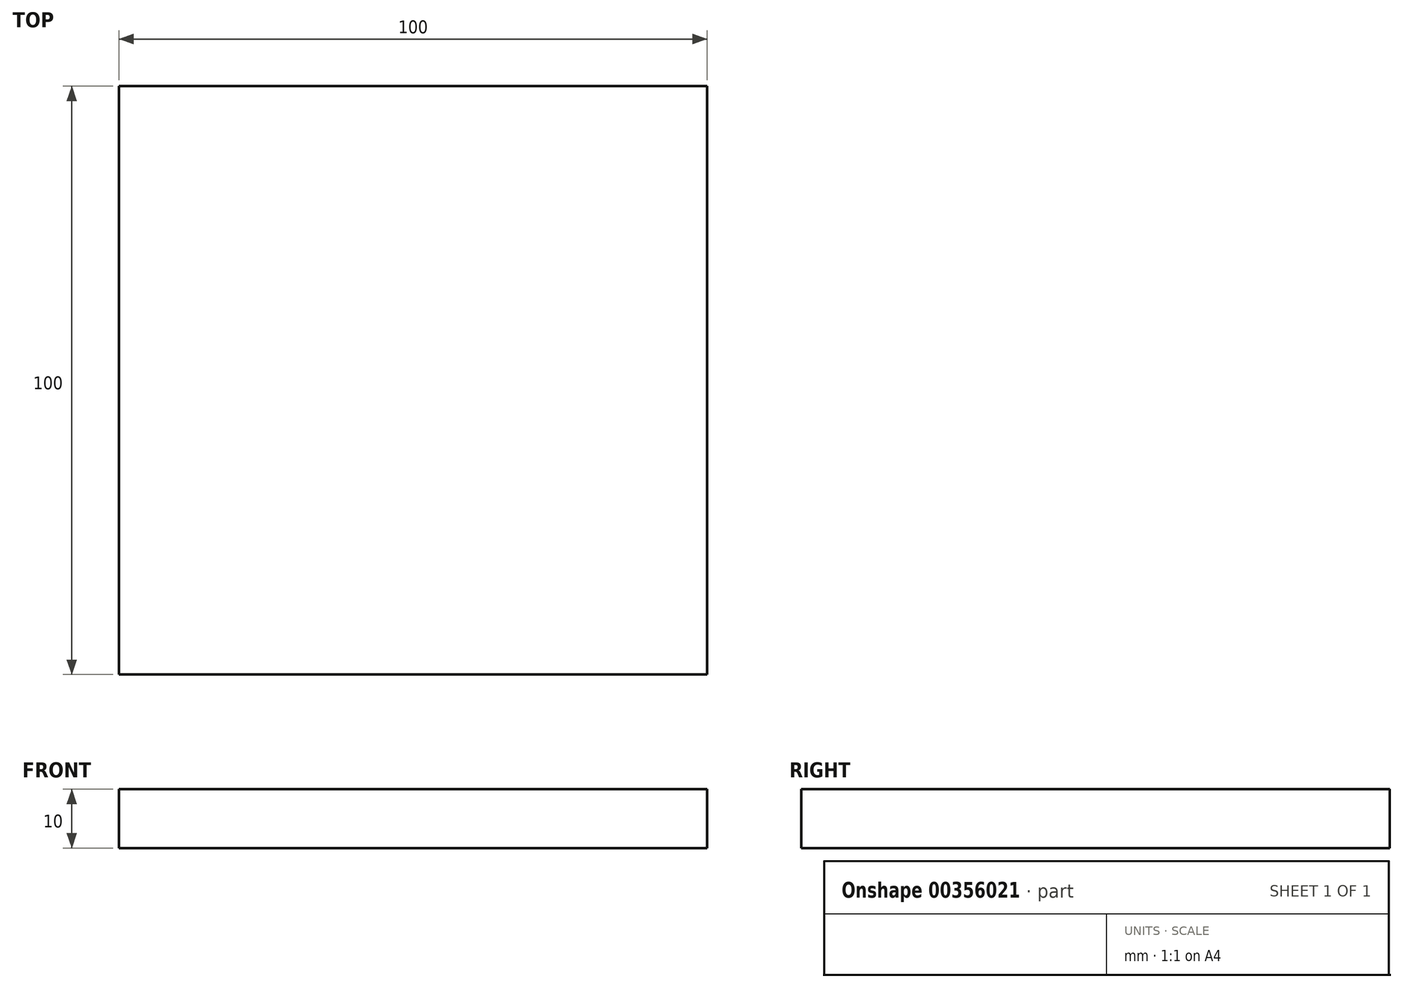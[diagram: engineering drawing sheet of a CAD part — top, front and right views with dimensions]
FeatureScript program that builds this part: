
annotation { "Feature Type Name" : "Feature", "Feature Type Description" : "" }
export const myFeature = defineFeature(function(context is Context, id is Id, definition is map)
    precondition{}
    {
        {
            var Q0;
            Q0=qCreatedBy(makeId("Top.planeOp"),FACE);
            var sketch = newSketch(context, id + "F0", { "sketchPlane" : qUnion([Q0])});
            skLineSegment(sketch, "E0.bottom", {"start": v(0, 0) * mm, "end": v(-100, 0) * mm});
            skLineSegment(sketch, "E0.top", {"start": v(0, 100) * mm, "end": v(-100, 100) * mm});
            skLineSegment(sketch, "E0.left", {"start": v(0, 0) * mm, "end": v(0, 100) * mm});
            skLineSegment(sketch, "E0.right", {"start": v(-100, 0) * mm, "end": v(-100, 100) * mm});
            skSolve(sketch);
        }
        {
            var Q0;
            Q0=makeQuery(id+"F0.imprint","IMPRINT",FACE,{"disambiguationData":[TD([[makeQuery(id+"F0.imprint","IMPRINT",EDGE,{"derivedFrom":sQuery(id+"F0.wireOp",EDGE,"E0.bottom")}),-1.0]])]});
            extrude(context, id + "F1", {"entities" : qUnion([Q0]), "depth" : 10 * mm});
        }
    });
